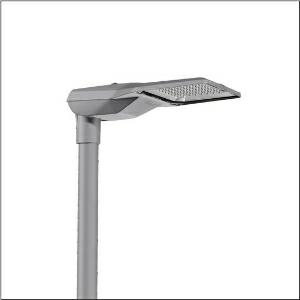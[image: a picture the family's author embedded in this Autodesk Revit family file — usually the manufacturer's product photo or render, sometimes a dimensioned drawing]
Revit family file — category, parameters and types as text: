
# Revit family: streetlight_sl_21_midi___p0_5a_5xe3v33s08nb_fb54
name_source: partatom
category: Lighting Fixtures
units: mm (PartAtom-declared; Revit-internal decimal feet)

## family parameters
Cut with Voids When Loaded = No
Host = Face
Light Source = No
Part Type = Normal
Room Calculation Point = No
Round Connector Dimension = Use Diameter
Shared = No

## types (1)
- --- (1 x LED, 22310 lm, 151.2 W, 3000K)
    Apparent Load = 151 VA
    CIE Flux Codes = 37 73 96 100 100
    Color Rendering = 70
    Color Temperature = 3000K
    Default Elevation = 1800 mm
    Description = Streetlight SL 21 midi, mast luminaire, primary light control with lens, of PMMA, primary optical cover: cover, of toughened safety glass, transparent, light distribution: P0.5a, light emission: direct distribution, primary light characteristic: asymmetric, installation type: post-top, side-entry, LED, High Power LED, rated luminous flux: 22.310lm, luminous efficacy: 148lm/W, light colour: 730, colour temperature: 3000K, control gear: D4i, control: pre-setting: logarithmic dimming characteristic, flexible luminous flux parameterisation, time-dependent luminous flux control, constant luminous flux control, overheat protection, mains connection: 230..240V, AC, 50/60Hz, start of lifetime: 151W, end of service life: 157W, reduction: 70W, luminaire housing, of diecast aluminium, powder-coated, Siteco® metallic grey (DB 702S), corrosivity category C5 mid according to DIN EN ISO 12944, multi-level sealing system, sealing non-destructively replaceable, inclination adjustable: 0°, 5°, 10°, 15°, please order mast flange separately, length: 644mm, width: 335mm, height: 110mm, mast flange for spigot size: 42mm (side-entry): 5XC10008XM4, 60/48mm (side-entry/post-top): 5XC10108XM2, 76/60mm (side-entry/post-top): 5XC10108XM1, mounting height: 4..8m, Smart Interface above, protection rating (complete): IP66, insulation class (complete): insulation class II (safety insulation), certification: CE, ENEC, ENEC+, VDE, impact resistance: IK09, permissible operating ambient temperature for outdoor applications: -40..+50°C, standard-compliant lighting for roads and squares, packaging unit: 1 piece

Light Distribution: P0.5a
    Height = 111 mm
    Lamp = 1 x LED
    Lamp Light Flux = 22310 lm
    Lamp Power = 151.2 W
    Lamp count = 1
    Length = 644 mm
    Luminous efficacy = 148 lm/W
    Manufacturer = Siteco
    ModVariant = No
    Model = 5XE3V33S08NB
    Number of Poles = 1
    OnlyDefault = Yes
    Power Factor = 1
    Product Name = Streetlight SL 21 midi | P0.5a
    Product group = mast luminaire | pylon top
    ProductGroupID = 6100
    Protection Class = Protection class II
    Protection Degree = IP 66
    RLX_Detail_Level = 1
    RLX_Emergency_Light_Flux = 0 lm
    RLX_Emergency_Type = 0
    RLX_Emergency_Type_DB = No
    RlxData = <blob elided: 90117 chars, md5=305b5901>
    Socket = socket
    Standby Power = 0 W
    System Light Flux = 22310 lm
    System Power = 151 W
    Type Comments = factory setting: luminous flux: 100 % | dim-lin: 254 | 802 mA
    Type Image = l_1004302.jpg
    URL = http://relux.com
    VarID = @adj_065972
    Voltage = 0 V
    Weight = 0.00 kg
    Width = 336 mm

## geometry (parser evidence)
native form markers: Blend x4, Sweep x12
no freeform markers — native parametric forms only
